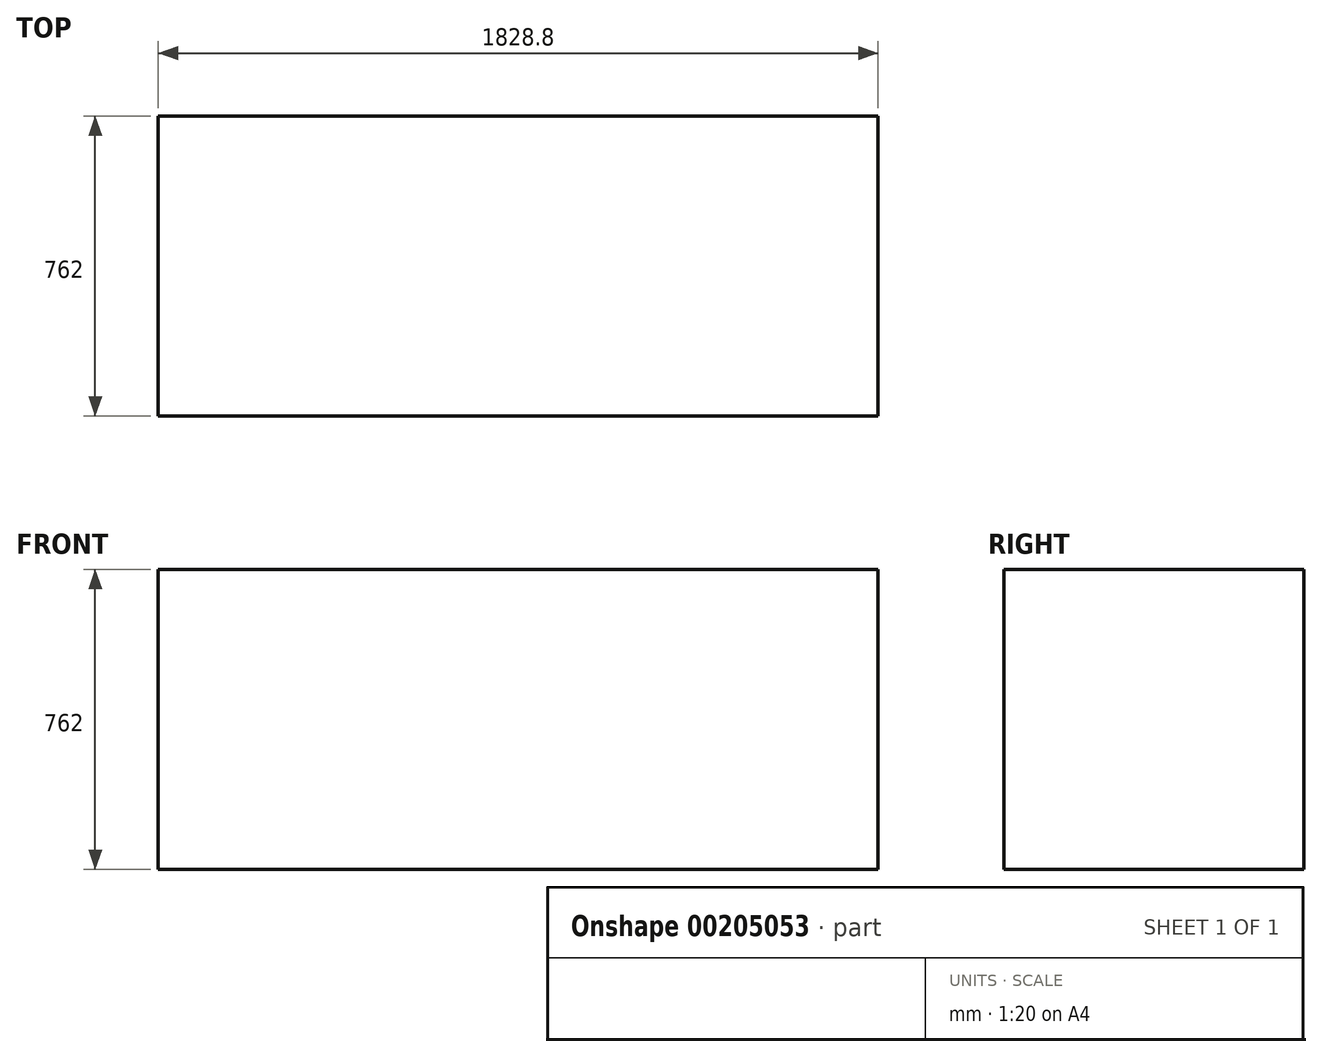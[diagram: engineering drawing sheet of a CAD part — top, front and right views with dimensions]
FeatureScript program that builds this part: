
annotation { "Feature Type Name" : "Feature", "Feature Type Description" : "" }
export const myFeature = defineFeature(function(context is Context, id is Id, definition is map)
    precondition{}
    {
        {
            var Q0;
            Q0=qCreatedBy(makeId("Top.planeOp"),FACE);
            var sketch = newSketch(context, id + "F0", { "sketchPlane" : qUnion([Q0])});
            skLineSegment(sketch, "E0.bottom", {"start": v(914.4, 381) * mm, "end": v(-914.4, 381) * mm});
            skLineSegment(sketch, "E0.top", {"start": v(914.4, -381) * mm, "end": v(-914.4, -381) * mm});
            skLineSegment(sketch, "E0.left", {"start": v(914.4, 381) * mm, "end": v(914.4, -381) * mm});
            skLineSegment(sketch, "E0.right", {"start": v(-914.4, 381) * mm, "end": v(-914.4, -381) * mm});
            skPoint(sketch, "E0.middle", {"position": v(0, 0) * mm});
            skSolve(sketch);
        }
        {
            var Q0;
            Q0=makeQuery(id+"F0.imprint","IMPRINT",FACE,{"disambiguationData":[TD([[makeQuery(id+"F0.imprint","IMPRINT",EDGE,{"derivedFrom":sQuery(id+"F0.wireOp",EDGE,"E0.bottom")}),1.0]])]});
            extrude(context, id + "F1", {"entities" : qUnion([Q0]), "depth" : 762 * mm});
        }
    });
